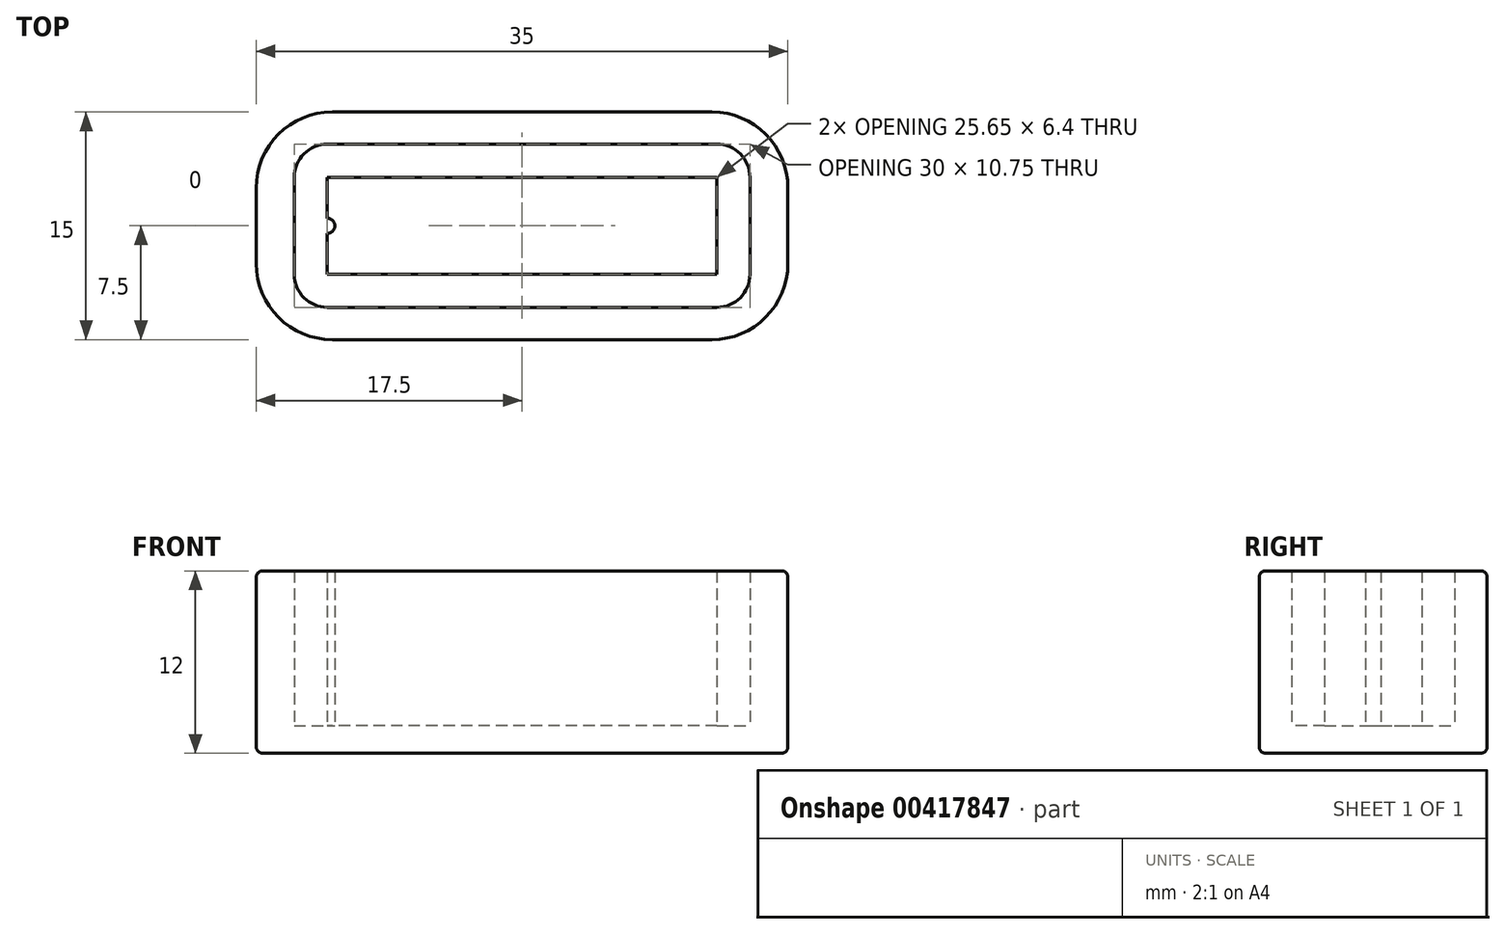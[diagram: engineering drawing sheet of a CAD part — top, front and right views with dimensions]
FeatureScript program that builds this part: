
annotation { "Feature Type Name" : "Feature", "Feature Type Description" : "" }
export const myFeature = defineFeature(function(context is Context, id is Id, definition is map)
    precondition{}
    {
        {
            var Q0;
            Q0=qCreatedBy(makeId("Top.planeOp"),FACE);
            var sketch = newSketch(context, id + "F0", { "sketchPlane" : qUnion([Q0])});
            skLineSegment(sketch, "E0.bottom", {"start": v(17.5, -7.5) * mm, "end": v(-17.5, -7.5) * mm});
            skLineSegment(sketch, "E0.top", {"start": v(17.5, 7.5) * mm, "end": v(-17.5, 7.5) * mm});
            skLineSegment(sketch, "E0.left", {"start": v(17.5, -7.5) * mm, "end": v(17.5, 7.5) * mm});
            skLineSegment(sketch, "E0.right", {"start": v(-17.5, -7.5) * mm, "end": v(-17.5, 7.5) * mm});
            skPoint(sketch, "E0.middle", {"position": v(0, 0) * mm});
            skSolve(sketch);
        }
        {
            var Q0;
            Q0=makeQuery(id+"F0.imprint","IMPRINT",FACE,{"disambiguationData":[TD([[makeQuery(id+"F0.imprint","IMPRINT",EDGE,{"derivedFrom":sQuery(id+"F0.wireOp",EDGE,"E0.bottom")}),-1.0]])]});
            extrude(context, id + "F1", {"entities" : qUnion([Q0]), "depth" : 12 * mm, "offsetDistance" : 25 * mm});
        }
        {
            var Q0;
            Q0=makeQuery(id+"F1.opExtrude","CAP_FACE",FACE,{"disambiguationData":[OSD([sQuery(id+"F0.wireOp",EDGE,"E0.bottom"),sQuery(id+"F0.wireOp",EDGE,"E0.top"),sQuery(id+"F0.wireOp",EDGE,"E0.left"),sQuery(id+"F0.wireOp",EDGE,"E0.right")])],"isStart":false});
            var sketch = newSketch(context, id + "F2", { "sketchPlane" : qUnion([Q0])});
            skLineSegment(sketch, "E1.bottom", {"start": v(15, -5.37) * mm, "end": v(-15, -5.38) * mm});
            skLineSegment(sketch, "E1.top", {"start": v(15, 5.38) * mm, "end": v(-15, 5.37) * mm});
            skLineSegment(sketch, "E1.left", {"start": v(15, -5.37) * mm, "end": v(15, 5.38) * mm});
            skLineSegment(sketch, "E1.right", {"start": v(-15, -5.38) * mm, "end": v(-15, 5.37) * mm});
            skPoint(sketch, "E1.middle", {"position": v(0, 0) * mm});
            skLineSegment(sketch, "E2.bottom", {"start": v(12.82, -3.2) * mm, "end": v(-12.82, -3.2) * mm});
            skLineSegment(sketch, "E2.top", {"start": v(12.82, 3.2) * mm, "end": v(-12.82, 3.2) * mm});
            skLineSegment(sketch, "E2.left", {"start": v(12.82, -3.2) * mm, "end": v(12.82, 3.2) * mm});
            skLineSegment(sketch, "E2.right", {"start": v(-12.82, -3.2) * mm, "end": v(-12.82, 3.2) * mm});
            skCircle(sketch, "E3", {"center": v(-12.82, 0) * mm, "radius": 0.5 * mm});
            skSolve(sketch);
        }
        {
            var Q0;
            Q0=makeQuery(id+"F2.imprint","IMPRINT",FACE,{"disambiguationData":[TD([[makeQuery(id+"F2.imprint","IMPRINT",EDGE,{"derivedFrom":sQuery(id+"F2.wireOp",EDGE,"E1.bottom")}),-1.0]])]});
            var Q1;
            {var subQ0=sQuery(id+"F2.wireOp",EDGE,"E3");var subQ1=sQuery(id+"F2.wireOp",EDGE,"E2.right");var subQ2=makeQuery(id+"F2.imprint","INTERSECT",VERTEX,{"disambiguationData":[OD(0.0)],"derivedFrom":[subQ1,subQ0]});Q1=makeQuery(id+"F2.imprint","IMPRINT",FACE,{"disambiguationData":[TD([[makeQuery(id+"F2.imprint","IMPRINT",EDGE,{"disambiguationData":[TD([[subQ2,-1.0]])],"derivedFrom":subQ1}),1.0]])]});}
            var Q2;
            {var subQ0=sQuery(id+"F2.wireOp",EDGE,"E3");var subQ1=sQuery(id+"F2.wireOp",EDGE,"E2.right");var subQ2=makeQuery(id+"F2.imprint","INTERSECT",VERTEX,{"disambiguationData":[OD(0.0)],"derivedFrom":[subQ1,subQ0]});Q2=makeQuery(id+"F2.imprint","IMPRINT",FACE,{"disambiguationData":[TD([[makeQuery(id+"F2.imprint","IMPRINT",EDGE,{"disambiguationData":[TD([[subQ2,-1.0]])],"derivedFrom":subQ1}),-1.0]])]});}
            extrude(context, id + "F3", {"entities" : qUnion([Q0, Q1, Q2]), "operationType" : NewBodyOperationType.REMOVE, "oppositeDirection" : true, "depth" : 10.2 * mm, "offsetDistance" : 25 * mm});
        }
        {
            var Q0;
            Q0=makeQuery(id+"F3.boolean.opBoolean","COPY",EDGE,{"derivedFrom":makeQuery(id+"F3.opExtrude","SWEPT_EDGE",EDGE,{"disambiguationData":[OSD([sQuery(id+"F2.wireOp",EDGE,"E1.top"),sQuery(id+"F2.wireOp",EDGE,"E1.right")])]})});
            var Q1;
            Q1=makeQuery(id+"F3.boolean.opBoolean","COPY",EDGE,{"derivedFrom":makeQuery(id+"F3.opExtrude","SWEPT_EDGE",EDGE,{"disambiguationData":[OSD([sQuery(id+"F2.wireOp",EDGE,"E1.top"),sQuery(id+"F2.wireOp",EDGE,"E1.left")])]})});
            var Q2;
            Q2=makeQuery(id+"F3.boolean.opBoolean","COPY",EDGE,{"derivedFrom":makeQuery(id+"F3.opExtrude","SWEPT_EDGE",EDGE,{"disambiguationData":[OSD([sQuery(id+"F2.wireOp",EDGE,"E1.bottom"),sQuery(id+"F2.wireOp",EDGE,"E1.left")])]})});
            var Q3;
            Q3=makeQuery(id+"F3.boolean.opBoolean","COPY",EDGE,{"derivedFrom":makeQuery(id+"F3.opExtrude","SWEPT_EDGE",EDGE,{"disambiguationData":[OSD([sQuery(id+"F2.wireOp",EDGE,"E1.bottom"),sQuery(id+"F2.wireOp",EDGE,"E1.right")])]})});
            fillet(context, id + "F4", {"entities" : qUnion([Q0, Q1, Q2, Q3]), "radius" : 2.17 * mm, "tangentPropagation" : true, "allowEdgeOverflow" : false});
        }
        {
            var Q0;
            Q0=makeQuery(id+"F1.opExtrude","SWEPT_EDGE",EDGE,{"disambiguationData":[OSD([sQuery(id+"F0.wireOp",EDGE,"E0.top"),sQuery(id+"F0.wireOp",EDGE,"E0.right")])]});
            var Q1;
            Q1=makeQuery(id+"F1.opExtrude","SWEPT_EDGE",EDGE,{"disambiguationData":[OSD([sQuery(id+"F0.wireOp",EDGE,"E0.bottom"),sQuery(id+"F0.wireOp",EDGE,"E0.right")])]});
            var Q2;
            Q2=makeQuery(id+"F1.opExtrude","SWEPT_EDGE",EDGE,{"disambiguationData":[OSD([sQuery(id+"F0.wireOp",EDGE,"E0.top"),sQuery(id+"F0.wireOp",EDGE,"E0.left")])]});
            var Q3;
            Q3=makeQuery(id+"F1.opExtrude","SWEPT_EDGE",EDGE,{"disambiguationData":[OSD([sQuery(id+"F0.wireOp",EDGE,"E0.bottom"),sQuery(id+"F0.wireOp",EDGE,"E0.left")])]});
            fillet(context, id + "F5", {"entities" : qUnion([Q0, Q1, Q2, Q3]), "radius" : 5 * mm, "tangentPropagation" : true, "allowEdgeOverflow" : false});
        }
        {
            var Q0;
            Q0=makeQuery(id+"F1.opExtrude","CAP_FACE",FACE,{"disambiguationData":[OSD([sQuery(id+"F0.wireOp",EDGE,"E0.bottom"),sQuery(id+"F0.wireOp",EDGE,"E0.top"),sQuery(id+"F0.wireOp",EDGE,"E0.left"),sQuery(id+"F0.wireOp",EDGE,"E0.right")])],"isStart":true});
            var Q1;
            {var subQ0=sQuery(id+"F0.wireOp",EDGE,"E0.left");var subQ1=sQuery(id+"F0.wireOp",EDGE,"E0.top");var subQ2=sQuery(id+"F0.wireOp",EDGE,"E0.right");var subQ3=sQuery(id+"F0.wireOp",EDGE,"E0.bottom");Q1=makeQuery(id+"F5.opFillet","BLEND_EDGE",EDGE,{"blendedFrom":[makeQuery(id+"F1.opExtrude","SWEPT_EDGE",EDGE,{"disambiguationData":[OSD([subQ3,subQ2])]}),makeQuery(id+"F3.boolean.opBoolean","SPLIT",FACE,{"disambiguationData":[TD([makeQuery(id+"F1.opExtrude","SWEPT_FACE",FACE,{"disambiguationData":[OSD([subQ3])]})])],"derivedFrom":makeQuery(id+"F1.opExtrude","CAP_FACE",FACE,{"disambiguationData":[OSD([subQ3,subQ1,subQ0,subQ2])],"isStart":false})})],"blendedInto":[makeQuery(id+"F3.boolean.opBoolean","SPLIT",FACE,{"disambiguationData":[TD([makeQuery(id+"F1.opExtrude","SWEPT_FACE",FACE,{"disambiguationData":[OSD([subQ3])]})])],"derivedFrom":makeQuery(id+"F1.opExtrude","CAP_FACE",FACE,{"disambiguationData":[OSD([subQ3,subQ1,subQ0,subQ2])],"isStart":false})})]});}
            fillet(context, id + "F6", {"entities" : qUnion([Q0, Q1]), "radius" : .4 * mm, "tangentPropagation" : true, "allowEdgeOverflow" : false});
        }
        {
            var Q0;
            Q0=makeQuery(id+"F3.boolean.opBoolean","COPY",FACE,{"derivedFrom":makeQuery(id+"F3.opExtrude","CAP_FACE",FACE,{"disambiguationData":[OSD([sQuery(id+"F2.wireOp",EDGE,"E1.bottom"),sQuery(id+"F2.wireOp",EDGE,"E1.top"),sQuery(id+"F2.wireOp",EDGE,"E1.left"),sQuery(id+"F2.wireOp",EDGE,"E1.right"),sQuery(id+"F2.wireOp",EDGE,"E2.bottom"),sQuery(id+"F2.wireOp",EDGE,"E2.top"),sQuery(id+"F2.wireOp",EDGE,"E2.left"),sQuery(id+"F2.wireOp",EDGE,"E2.right"),sQuery(id+"F2.wireOp",EDGE,"E3")])],"isStart":false})});
            extrude(context, id + "F7", {"entities" : qUnion([Q0]), "depth" : 10.2 * mm, "offsetDistance" : 25 * mm});
        }
    });
